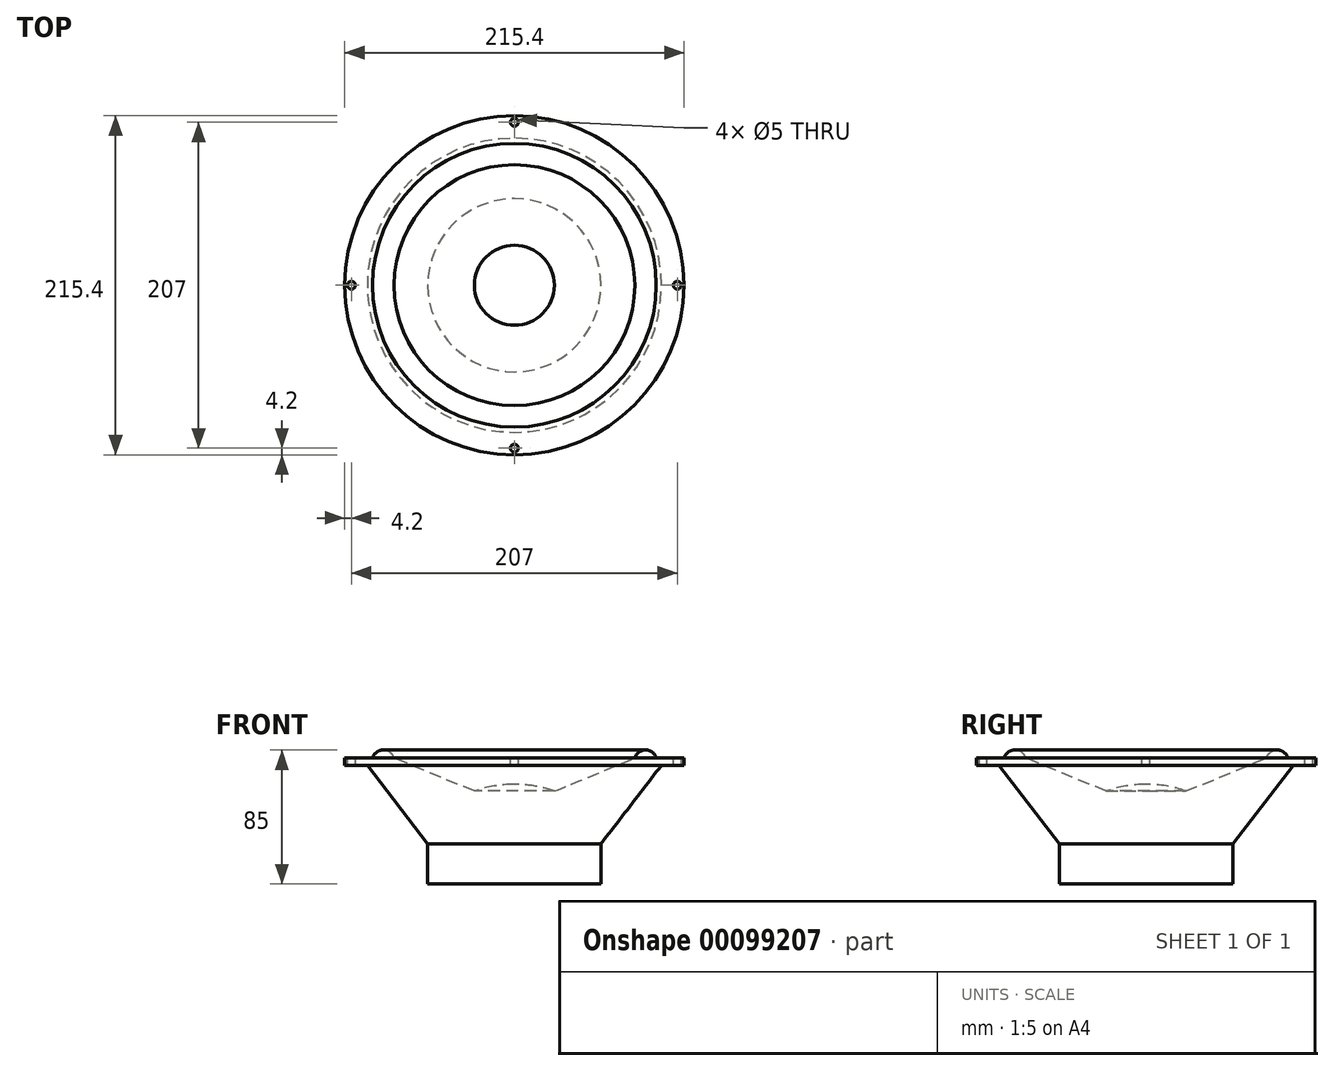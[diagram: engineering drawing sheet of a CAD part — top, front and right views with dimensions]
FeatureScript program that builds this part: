
annotation { "Feature Type Name" : "Feature", "Feature Type Description" : "" }
export const myFeature = defineFeature(function(context is Context, id is Id, definition is map)
    precondition{}
    {
        {
            var Q0;
            Q0=qCreatedBy(makeId("Front.planeOp"),FACE);
            var sketch = newSketch(context, id + "F0", { "sketchPlane" : qUnion([Q0])});
            skLineSegment(sketch, "E0", {"start": v(0, 63.2) * mm, "end": v(0, 0) * mm});
            skLineSegment(sketch, "E1", {"start": v(0, 0) * mm, "end": v(-55, 0) * mm});
            skLineSegment(sketch, "E2", {"start": v(-55, 0) * mm, "end": v(-55, 25.4) * mm});
            skArc(sketch, "E3", {"start": v(0, 63.2) * mm, "mid": v(-12.88, 62.1) * mm, "end": v(-25.4, 58.88) * mm});
            skLineSegment(sketch, "E4", {"start": v(-55, 25.4) * mm, "end": v(-93.4, 75.3) * mm});
            skLineSegment(sketch, "E5", {"start": v(-93.4, 75.3) * mm, "end": v(-107.7, 75.3) * mm});
            skLineSegment(sketch, "E6", {"start": v(-107.7, 75.3) * mm, "end": v(-107.7, 80) * mm});
            skLineSegment(sketch, "E7", {"start": v(-107.7, 80) * mm, "end": v(-90.08, 80) * mm});
            skArc(sketch, "E8", {"start": v(-76.5, 80) * mm, "mid": v(-83.3, 85) * mm, "end": v(-90.08, 80) * mm});
            skLineSegment(sketch, "E9", {"start": v(-76.5, 80) * mm, "end": v(-25.4, 58.88) * mm});
            skSolve(sketch);
        }
        {
            var Q0;
            Q0 = qSketchRegion(id + "F0", true);
            var Q1;
            Q1=sQuery(id+"F0.wireOp",EDGE,"E0");
            revolve(context, id + "F1", {"entities" : qUnion([Q0]), "axis" : qUnion([Q1]), "revolveType" : RevolveType.FULL});
        }
        {
            var Q0;
            Q0=makeQuery(id+"F1.opRevolve","SWEPT_FACE",FACE,{"disambiguationData":[OSD([sQuery(id+"F0.wireOp",EDGE,"E7")])]});
            var sketch = newSketch(context, id + "F2", { "sketchPlane" : qUnion([Q0])});
            skCircle(sketch, "E10", {"center": v(-103.5, 0) * mm, "radius": 2.5 * mm});
            skCircle(sketch, "E11", {"center": v(0, 0) * mm, "radius": 103.5 * mm, "construction": true});
            skCircle(sketch, "E12", {"center": v(0, 103.5) * mm, "radius": 2.5 * mm});
            skCircle(sketch, "E13", {"center": v(103.5, 0) * mm, "radius": 2.5 * mm});
            skCircle(sketch, "E14", {"center": v(0, -103.5) * mm, "radius": 2.5 * mm});
            skSolve(sketch);
        }
        {
            var Q0;
            Q0 = qSketchRegion(id + "F2", true);
            extrude(context, id + "F3", {"entities" : qUnion([Q0]), "operationType" : NewBodyOperationType.REMOVE, "endBound" : BoundingType.UP_TO_NEXT, "oppositeDirection" : true, "depth" : 25.4 * mm});
        }
    });
